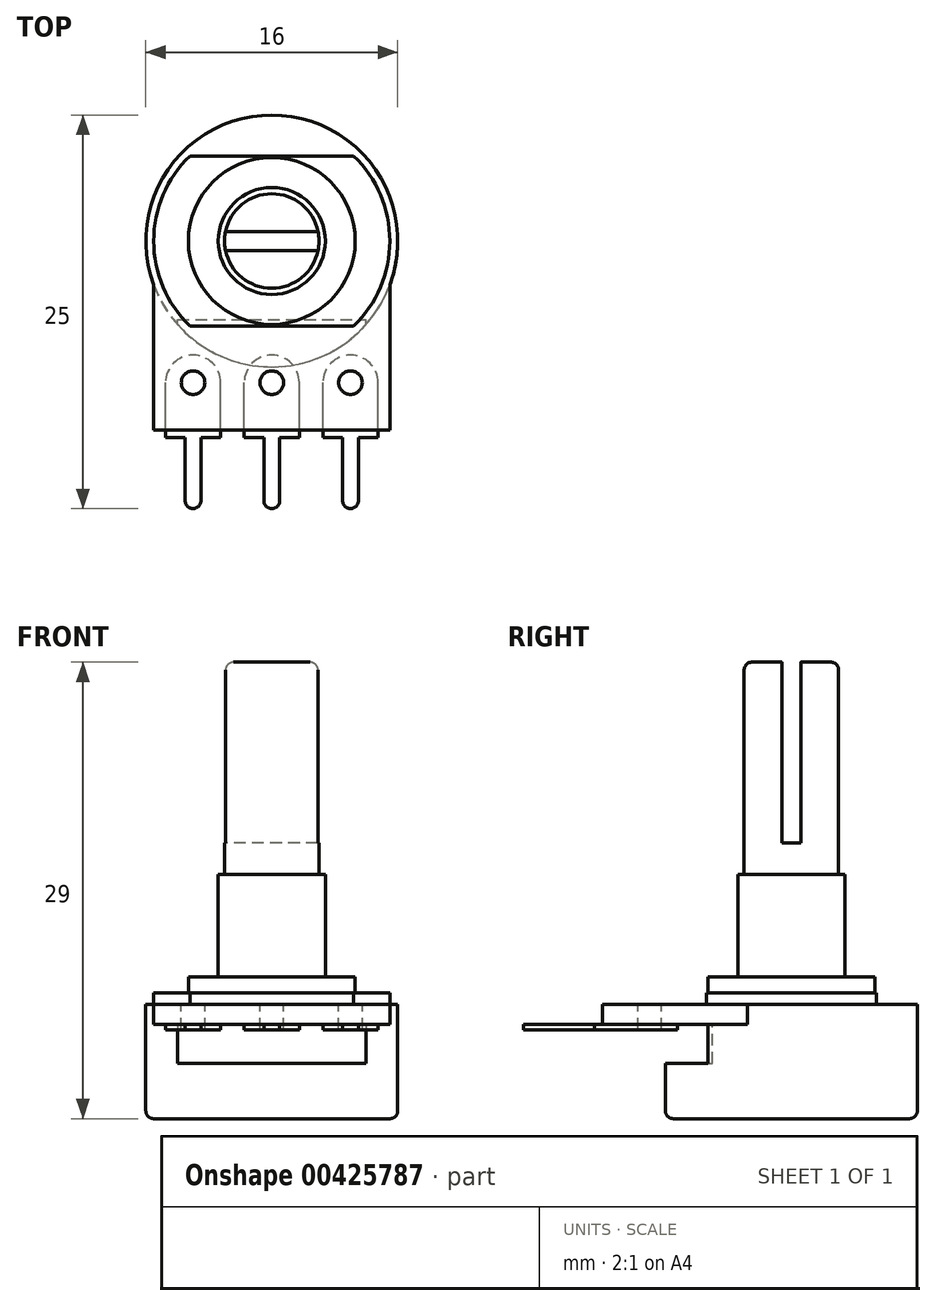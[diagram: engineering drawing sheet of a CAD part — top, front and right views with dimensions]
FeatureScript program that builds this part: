
annotation { "Feature Type Name" : "Feature", "Feature Type Description" : "" }
export const myFeature = defineFeature(function(context is Context, id is Id, definition is map)
    precondition{}
    {
        {
            var Q0;
            Q0=qCreatedBy(makeId("Top.planeOp"),FACE);
            var sketch = newSketch(context, id + "F0", { "sketchPlane" : qUnion([Q0])});
            skCircle(sketch, "E0", {"center": v(0, 0) * mm, "radius": 8 * mm});
            skSolve(sketch);
        }
        {
            var Q0;
            Q0 = qSketchRegion(id + "F0", true);
            extrude(context, id + "F1", {"entities" : qUnion([Q0]), "depth" : 6 * mm});
        }
        {
            var Q0;
            Q0=makeQuery(id+"F1.opExtrude","CAP_FACE",FACE,{"disambiguationData":[OSD([sQuery(id+"F0.wireOp",EDGE,"E0")])],"isStart":false});
            var sketch = newSketch(context, id + "F2", { "sketchPlane" : qUnion([Q0])});
            skLineSegment(sketch, "E1", {"start": v(0, 0) * mm, "end": v(0, -19.82) * mm, "construction": true});
            skLineSegment(sketch, "E2", {"start": v(7.5, -12) * mm, "end": v(7.5, -2.78) * mm});
            skLineSegment(sketch, "E3.MirrorCS", {"start": v(-7.5, -12) * mm, "end": v(-7.5, -2.78) * mm});
            skLineSegment(sketch, "E4", {"start": v(-7.5, -12) * mm, "end": v(7.5, -12) * mm});
            skArc(sketch, "E5", {"start": v(-7.5, -2.78) * mm, "mid": v(0, 8) * mm, "end": v(7.5, -2.78) * mm});
            skSolve(sketch);
        }
        {
            var Q0;
            Q0 = qSketchRegion(id + "F2", true);
            extrude(context, id + "F3", {"entities" : qUnion([Q0]), "operationType" : NewBodyOperationType.ADD, "depth" : 1.25 * mm});
        }
        {
            var Q0;
            Q0=makeQuery(id+"F3.opExtrude","CAP_FACE",FACE,{"disambiguationData":[OSD([sQuery(id+"F2.wireOp",EDGE,"E2"),sQuery(id+"F2.wireOp",EDGE,"E3.MirrorCS"),sQuery(id+"F2.wireOp",EDGE,"E4"),sQuery(id+"F2.wireOp",EDGE,"E5")])],"isStart":false});
            var sketch = newSketch(context, id + "F4", { "sketchPlane" : qUnion([Q0])});
            skArc(sketch, "E6", {"start": v(-5.2, 5.4) * mm, "mid": v(-7.5, 0) * mm, "end": v(-5.2, -5.4) * mm});
            skLineSegment(sketch, "E7", {"start": v(-5.2, 5.4) * mm, "end": v(5.2, 5.4) * mm});
            skLineSegment(sketch, "E8", {"start": v(-5.2, -5.4) * mm, "end": v(5.2, -5.4) * mm});
            skArc(sketch, "E9.trimOffspring", {"start": v(5.2, -5.4) * mm, "mid": v(7.5, 0) * mm, "end": v(5.2, 5.4) * mm});
            skSolve(sketch);
        }
        {
            var Q0;
            Q0 = qSketchRegion(id + "F4", true);
            extrude(context, id + "F5", {"entities" : qUnion([Q0]), "operationType" : NewBodyOperationType.ADD, "depth" : 0.75 * mm});
        }
        {
            var Q0;
            Q0=makeQuery(id+"F5.opExtrude","CAP_FACE",FACE,{"disambiguationData":[OSD([sQuery(id+"F4.wireOp",EDGE,"E6"),sQuery(id+"F4.wireOp",EDGE,"E7"),sQuery(id+"F4.wireOp",EDGE,"E8"),sQuery(id+"F4.wireOp",EDGE,"E9.trimOffspring")])],"isStart":false});
            var sketch = newSketch(context, id + "F6", { "sketchPlane" : qUnion([Q0])});
            skCircle(sketch, "E10", {"center": v(0, 0) * mm, "radius": 5.3 * mm});
            skSolve(sketch);
        }
        {
            var Q0;
            Q0 = qSketchRegion(id + "F6", true);
            extrude(context, id + "F7", {"entities" : qUnion([Q0]), "operationType" : NewBodyOperationType.ADD, "depth" : 1 * mm});
        }
        {
            var Q0;
            Q0=makeQuery(id+"F7.opExtrude","CAP_FACE",FACE,{"disambiguationData":[OSD([sQuery(id+"F6.wireOp",EDGE,"E10")])],"isStart":false});
            var sketch = newSketch(context, id + "F8", { "sketchPlane" : qUnion([Q0])});
            skCircle(sketch, "E11", {"center": v(0, 0) * mm, "radius": 3.4 * mm});
            skSolve(sketch);
        }
        {
            var Q0;
            Q0 = qSketchRegion(id + "F8", true);
            extrude(context, id + "F9", {"entities" : qUnion([Q0]), "operationType" : NewBodyOperationType.ADD, "depth" : 6.5 * mm});
        }
        {
            var Q0;
            Q0=makeQuery(id+"F9.opExtrude","CAP_FACE",FACE,{"disambiguationData":[OSD([sQuery(id+"F8.wireOp",EDGE,"E11")])],"isStart":false});
            var sketch = newSketch(context, id + "F10", { "sketchPlane" : qUnion([Q0])});
            skCircle(sketch, "E12", {"center": v(0, 0) * mm, "radius": 3 * mm});
            skSolve(sketch);
        }
        {
            var Q0;
            Q0 = qSketchRegion(id + "F10", true);
            extrude(context, id + "F11", {"entities" : qUnion([Q0]), "operationType" : NewBodyOperationType.ADD, "depth" : 13.5 * mm});
        }
        {
            var Q0;
            Q0=makeQuery(id+"F3.opExtrude","CAP_FACE",FACE,{"disambiguationData":[OSD([sQuery(id+"F2.wireOp",EDGE,"E2"),sQuery(id+"F2.wireOp",EDGE,"E3.MirrorCS"),sQuery(id+"F2.wireOp",EDGE,"E4"),sQuery(id+"F2.wireOp",EDGE,"E5")])],"isStart":true});
            var sketch = newSketch(context, id + "F12", { "sketchPlane" : qUnion([Q0])});
            skLineSegment(sketch, "E13.bottom", {"start": v(-6, 11) * mm, "end": v(6, 11) * mm});
            skLineSegment(sketch, "E13.top", {"start": v(-6, 5) * mm, "end": v(6, 5) * mm});
            skLineSegment(sketch, "E13.left", {"start": v(-6, 11) * mm, "end": v(-6, 5) * mm});
            skLineSegment(sketch, "E13.right", {"start": v(6, 11) * mm, "end": v(6, 5) * mm});
            skSolve(sketch);
        }
        {
            var Q0;
            Q0 = qSketchRegion(id + "F12", true);
            extrude(context, id + "F13", {"entities" : qUnion([Q0]), "operationType" : NewBodyOperationType.REMOVE, "depth" : 2.5 * mm});
        }
        {
            var Q0;
            Q0=makeQuery(id+"F3.opExtrude","CAP_FACE",FACE,{"disambiguationData":[OSD([sQuery(id+"F2.wireOp",EDGE,"E2"),sQuery(id+"F2.wireOp",EDGE,"E3.MirrorCS"),sQuery(id+"F2.wireOp",EDGE,"E4"),sQuery(id+"F2.wireOp",EDGE,"E5")])],"isStart":false});
            var sketch = newSketch(context, id + "F14", { "sketchPlane" : qUnion([Q0])});
            skLineSegment(sketch, "E14", {"start": v(-14.03, -9) * mm, "end": v(14.12, -9) * mm, "construction": true});
            skPoint(sketch, "E15.0", {"position": v(0, 8) * mm});
            skCircle(sketch, "E16", {"center": v(-5, -9) * mm, "radius": 0.75 * mm});
            skCircle(sketch, "E17", {"center": v(0, -9) * mm, "radius": 0.75 * mm});
            skCircle(sketch, "E18", {"center": v(5, -9) * mm, "radius": 0.75 * mm});
            skSolve(sketch);
        }
        {
            var Q0;
            Q0 = qSketchRegion(id + "F14", true);
            extrude(context, id + "F15", {"entities" : qUnion([Q0]), "operationType" : NewBodyOperationType.REMOVE, "oppositeDirection" : true, "depth" : 25 * mm});
        }
        {
            var Q0;
            Q0=makeQuery(id+"F13.boolean.opBoolean","MERGE",FACE,{"derivedFrom":[makeQuery(id+"F3.opExtrude","CAP_FACE",FACE,{"disambiguationData":[OSD([sQuery(id+"F2.wireOp",EDGE,"E2"),sQuery(id+"F2.wireOp",EDGE,"E3.MirrorCS"),sQuery(id+"F2.wireOp",EDGE,"E4"),sQuery(id+"F2.wireOp",EDGE,"E5")])],"isStart":true}),makeQuery(id+"F13.opExtrude","CAP_FACE",FACE,{"disambiguationData":[OSD([sQuery(id+"F12.wireOp",EDGE,"E13.bottom"),sQuery(id+"F12.wireOp",EDGE,"E13.top"),sQuery(id+"F12.wireOp",EDGE,"E13.left"),sQuery(id+"F12.wireOp",EDGE,"E13.right")])],"isStart":true})]});
            var sketch = newSketch(context, id + "F16", { "sketchPlane" : qUnion([Q0])});
            skLineSegment(sketch, "E19", {"start": v(3.25, 12.5) * mm, "end": v(4.5, 12.5) * mm});
            skLineSegment(sketch, "E20", {"start": v(6.75, 12.5) * mm, "end": v(6.75, 9) * mm});
            skLineSegment(sketch, "E21", {"start": v(3.25, 12.5) * mm, "end": v(3.25, 9) * mm});
            skCircle(sketch, "E22.0", {"center": v(5, 9) * mm, "radius": 0.75 * mm});
            skArc(sketch, "E23", {"start": v(3.25, 9) * mm, "mid": v(5, 7.25) * mm, "end": v(6.75, 9) * mm});
            skLineSegment(sketch, "E24", {"start": v(4.5, 12.5) * mm, "end": v(4.5, 16.5) * mm});
            skLineSegment(sketch, "E25", {"start": v(5, 17) * mm, "end": v(5, 17) * mm});
            skLineSegment(sketch, "E26", {"start": v(5.5, 16.5) * mm, "end": v(5.5, 12.5) * mm});
            skLineSegment(sketch, "E27.trimOffspring", {"start": v(5.5, 12.5) * mm, "end": v(6.75, 12.5) * mm});
            skPoint(sketch, "E28.visualSharp", {"position": v(4.5, 17) * mm});
            skArc(sketch, "E28.filletArc", {"start": v(5, 17) * mm, "mid": v(4.65, 16.85) * mm, "end": v(4.5, 16.5) * mm});
            skPoint(sketch, "E29.visualSharp", {"position": v(5.5, 17) * mm});
            skArc(sketch, "E29.filletArc", {"start": v(5.5, 16.5) * mm, "mid": v(5.35, 16.85) * mm, "end": v(5, 17) * mm});
            skLineSegment(sketch, "E30.1.0.0", {"start": v(-0.5, 12.5) * mm, "end": v(-0.5, 16.5) * mm});
            skArc(sketch, "E30.1.0.1", {"start": v(0, 17) * mm, "mid": v(-0.35, 16.85) * mm, "end": v(-0.5, 16.5) * mm});
            skArc(sketch, "E30.1.0.2", {"start": v(0.5, 16.5) * mm, "mid": v(0.35, 16.85) * mm, "end": v(0, 17) * mm});
            skLineSegment(sketch, "E30.1.0.3", {"start": v(0.5, 16.5) * mm, "end": v(0.5, 12.5) * mm});
            skLineSegment(sketch, "E30.1.0.4", {"start": v(0.5, 12.5) * mm, "end": v(1.75, 12.5) * mm});
            skLineSegment(sketch, "E30.1.0.5", {"start": v(1.75, 12.5) * mm, "end": v(1.75, 9) * mm});
            skLineSegment(sketch, "E30.1.0.6", {"start": v(-1.75, 12.5) * mm, "end": v(-0.5, 12.5) * mm});
            skLineSegment(sketch, "E30.1.0.7", {"start": v(-1.75, 12.5) * mm, "end": v(-1.75, 9) * mm});
            skArc(sketch, "E30.1.0.8", {"start": v(-1.75, 9) * mm, "mid": v(0, 7.25) * mm, "end": v(1.75, 9) * mm});
            skCircle(sketch, "E30.1.0.9", {"center": v(0, 9) * mm, "radius": 0.75 * mm});
            skLineSegment(sketch, "E30.2.0.0", {"start": v(-5.5, 12.5) * mm, "end": v(-5.5, 16.5) * mm});
            skArc(sketch, "E30.2.0.1", {"start": v(-5, 17) * mm, "mid": v(-5.35, 16.85) * mm, "end": v(-5.5, 16.5) * mm});
            skArc(sketch, "E30.2.0.2", {"start": v(-4.5, 16.5) * mm, "mid": v(-4.65, 16.85) * mm, "end": v(-5, 17) * mm});
            skLineSegment(sketch, "E30.2.0.3", {"start": v(-4.5, 16.5) * mm, "end": v(-4.5, 12.5) * mm});
            skLineSegment(sketch, "E30.2.0.4", {"start": v(-4.5, 12.5) * mm, "end": v(-3.25, 12.5) * mm});
            skLineSegment(sketch, "E30.2.0.5", {"start": v(-3.25, 12.5) * mm, "end": v(-3.25, 9) * mm});
            skLineSegment(sketch, "E30.2.0.6", {"start": v(-6.75, 12.5) * mm, "end": v(-5.5, 12.5) * mm});
            skLineSegment(sketch, "E30.2.0.7", {"start": v(-6.75, 12.5) * mm, "end": v(-6.75, 9) * mm});
            skArc(sketch, "E30.2.0.8", {"start": v(-6.75, 9) * mm, "mid": v(-5, 7.25) * mm, "end": v(-3.25, 9) * mm});
            skCircle(sketch, "E30.2.0.9", {"center": v(-5, 9) * mm, "radius": 0.75 * mm});
            skLineSegment(sketch, "E30.direction1", {"start": v(4.5, 12.5) * mm, "end": v(-0.5, 12.5) * mm, "construction": true});
            skSolve(sketch);
        }
        {
            var Q0;
            Q0 = qSketchRegion(id + "F16", true);
            extrude(context, id + "F17", {"entities" : qUnion([Q0]), "operationType" : NewBodyOperationType.ADD, "depth" : 0.35 * mm});
        }
        {
            var Q0;
            Q0=makeQuery(id+"F11.opExtrude","CAP_FACE",FACE,{"disambiguationData":[OSD([sQuery(id+"F10.wireOp",EDGE,"E12")])],"isStart":false});
            var Q1;
            Q1=makeQuery(id+"F1.opExtrude","CAP_FACE",FACE,{"disambiguationData":[OSD([sQuery(id+"F0.wireOp",EDGE,"E0")])],"isStart":true});
            fillet(context, id + "F18", {"entities" : qUnion([Q0, Q1]), "radius" : 0.5 * mm, "tangentPropagation" : true, "allowEdgeOverflow" : false});
        }
        {
            var Q0;
            Q0=makeQuery(id+"F11.opExtrude","CAP_FACE",FACE,{"disambiguationData":[OSD([sQuery(id+"F10.wireOp",EDGE,"E12")])],"isStart":false});
            var sketch = newSketch(context, id + "F19", { "sketchPlane" : qUnion([Q0])});
            skLineSegment(sketch, "E31.bottom", {"start": v(5.94, 0.6) * mm, "end": v(-5.94, 0.6) * mm});
            skLineSegment(sketch, "E31.top", {"start": v(5.94, -0.6) * mm, "end": v(-5.94, -0.6) * mm});
            skLineSegment(sketch, "E31.left", {"start": v(5.94, 0.6) * mm, "end": v(5.94, -0.6) * mm});
            skLineSegment(sketch, "E31.right", {"start": v(-5.94, 0.6) * mm, "end": v(-5.94, -0.6) * mm});
            skPoint(sketch, "E31.middle", {"position": v(0, 0) * mm});
            skSolve(sketch);
        }
        {
            var Q0;
            Q0 = qSketchRegion(id + "F19", true);
            extrude(context, id + "F20", {"entities" : qUnion([Q0]), "operationType" : NewBodyOperationType.REMOVE, "oppositeDirection" : true, "depth" : 11.5 * mm});
        }
    });
